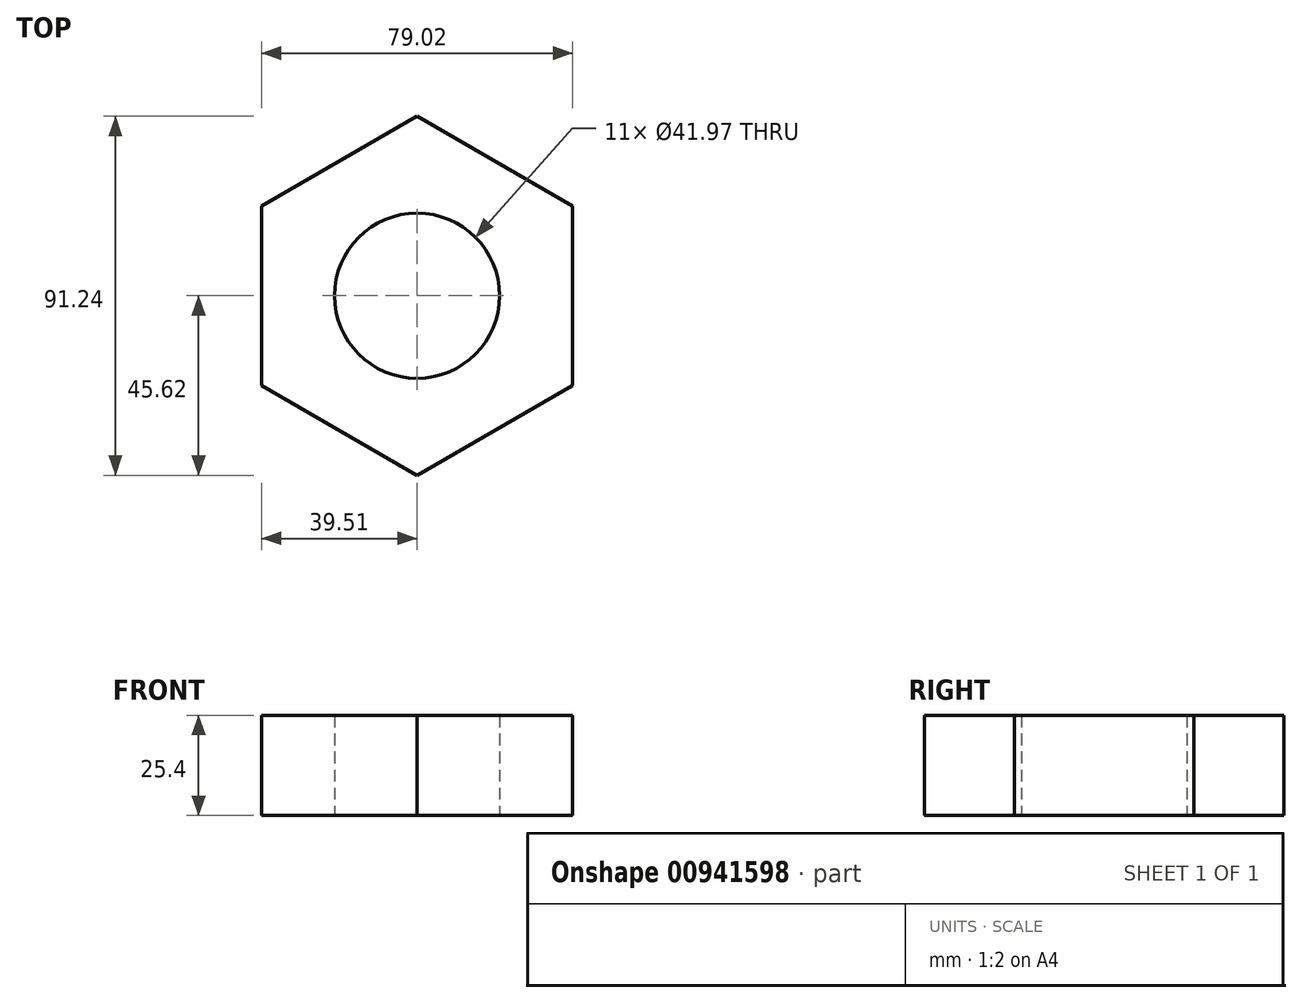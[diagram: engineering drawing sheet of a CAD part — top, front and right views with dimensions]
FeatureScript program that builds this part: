
annotation { "Feature Type Name" : "Feature", "Feature Type Description" : "" }
export const myFeature = defineFeature(function(context is Context, id is Id, definition is map)
    precondition{}
    {
        {
            var Q0;
            Q0=qCreatedBy(makeId("Top.planeOp"),FACE);
            var sketch = newSketch(context, id + "F0", { "sketchPlane" : qUnion([Q0])});
            skCircle(sketch, "E0.cCircle", {"center": v(0, 0) * mm, "radius": 39.5 * mm, "construction": true});
            skLineSegment(sketch, "E0.0", {"start": v(-39.5, 22.8) * mm, "end": v(0, 45.62) * mm});
            skLineSegment(sketch, "E0.1", {"start": v(0, 45.62) * mm, "end": v(39.5, 22.8) * mm});
            skLineSegment(sketch, "E0.2", {"start": v(39.5, 22.8) * mm, "end": v(39.5, -22.8) * mm});
            skLineSegment(sketch, "E0.3", {"start": v(39.5, -22.8) * mm, "end": v(0, -45.62) * mm});
            skLineSegment(sketch, "E0.4", {"start": v(0, -45.62) * mm, "end": v(-39.5, -22.8) * mm});
            skLineSegment(sketch, "E0.5", {"start": v(-39.5, -22.8) * mm, "end": v(-39.5, 22.8) * mm});
            skPoint(sketch, "E0.0.midPoint", {"position": v(-19.75, 34.21) * mm});
            skCircle(sketch, "E1", {"center": v(0, 0) * mm, "radius": 20.98 * mm});
            skSolve(sketch);
        }
        {
            var Q0;
            Q0=makeQuery(id+"F0.imprint","IMPRINT",FACE,{"disambiguationData":[TD([[makeQuery(id+"F0.imprint","IMPRINT",EDGE,{"derivedFrom":sQuery(id+"F0.wireOp",EDGE,"E0.0")}),-1.0]])]});
            extrude(context, id + "F1", {"entities" : qUnion([Q0]), "depth" : 25.4 * mm, "offsetDistance" : 25.4 * mm});
        }
    });
